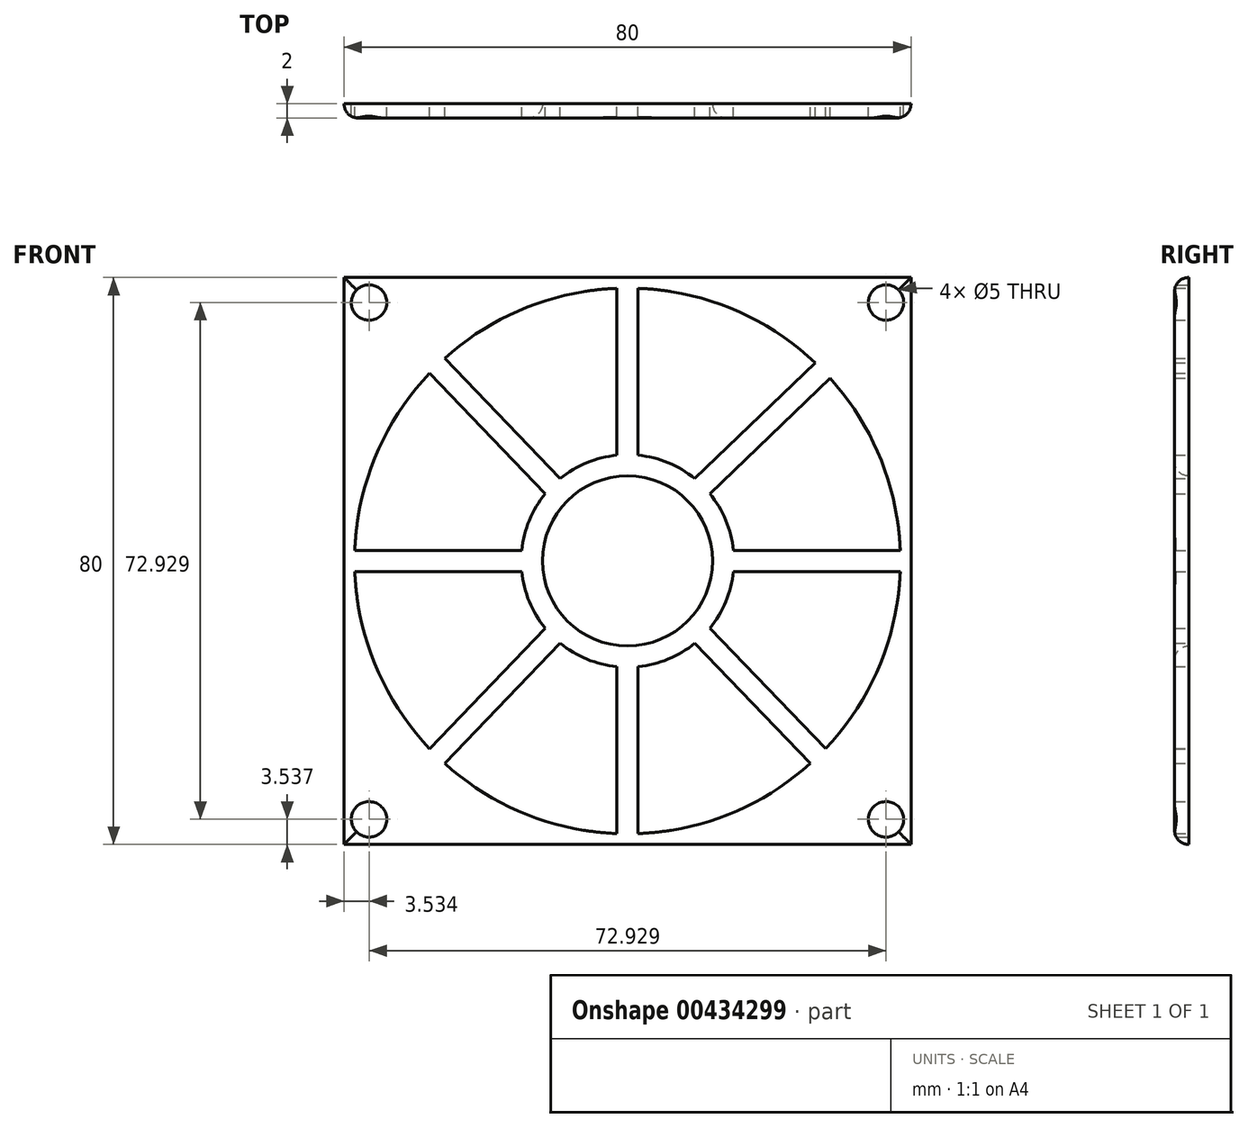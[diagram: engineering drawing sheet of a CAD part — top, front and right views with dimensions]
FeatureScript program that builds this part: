
annotation { "Feature Type Name" : "Feature", "Feature Type Description" : "" }
export const myFeature = defineFeature(function(context is Context, id is Id, definition is map)
    precondition{}
    {
        {
            var Q0;
            Q0=qCreatedBy(makeId("Front.planeOp"),FACE);
            var sketch = newSketch(context, id + "F0", { "sketchPlane" : qUnion([Q0])});
            skLineSegment(sketch, "E0.bottom", {"start": v(-40, 40.17) * mm, "end": v(40, 40.17) * mm});
            skLineSegment(sketch, "E0.top", {"start": v(-40, -39.83) * mm, "end": v(40, -39.83) * mm});
            skLineSegment(sketch, "E0.left", {"start": v(-40, 40.17) * mm, "end": v(-40, -39.83) * mm});
            skLineSegment(sketch, "E0.right", {"start": v(40, 40.17) * mm, "end": v(40, -39.83) * mm});
            skCircle(sketch, "E1", {"center": v(0, 0.17) * mm, "radius": 38.5 * mm});
            skCircle(sketch, "E2", {"center": v(0, 0.17) * mm, "radius": 15 * mm});
            skLineSegment(sketch, "E3", {"start": v(0, 38.67) * mm, "end": v(0, 15.17) * mm});
            skLineSegment(sketch, "E4", {"start": v(15, 0.17) * mm, "end": v(38.5, 0.17) * mm});
            skLineSegment(sketch, "E5", {"start": v(0, -14.83) * mm, "end": v(0, -38.33) * mm});
            skLineSegment(sketch, "E6", {"start": v(-15, 0.17) * mm, "end": v(-38.5, 0.17) * mm});
            skLineSegment(sketch, "E7", {"start": v(-1.5, -14.75) * mm, "end": v(-1.5, -38.3) * mm});
            skLineSegment(sketch, "E8", {"start": v(1.5, -14.75) * mm, "end": v(1.5, -38.3) * mm});
            skLineSegment(sketch, "E9", {"start": v(9.5, -11.44) * mm, "end": v(25.78, -28.42) * mm});
            skLineSegment(sketch, "E10", {"start": v(11.61, -9.32) * mm, "end": v(27.93, -26.33) * mm});
            skLineSegment(sketch, "E11", {"start": v(14.92, -1.33) * mm, "end": v(38.47, -1.33) * mm});
            skLineSegment(sketch, "E12", {"start": v(14.92, 1.67) * mm, "end": v(38.47, 1.67) * mm});
            skLineSegment(sketch, "E13", {"start": v(11.61, 9.67) * mm, "end": v(28.6, 25.95) * mm});
            skLineSegment(sketch, "E14", {"start": v(9.5, 11.79) * mm, "end": v(26.5, 28.1) * mm});
            skLineSegment(sketch, "E15", {"start": v(1.5, 15.1) * mm, "end": v(1.5, 38.64) * mm});
            skLineSegment(sketch, "E16", {"start": v(-1.5, 38.64) * mm, "end": v(-1.5, 15.1) * mm});
            skLineSegment(sketch, "E17", {"start": v(-9.5, 11.78) * mm, "end": v(-25.78, 28.76) * mm});
            skLineSegment(sketch, "E18", {"start": v(-11.62, 9.66) * mm, "end": v(-27.93, 26.67) * mm});
            skLineSegment(sketch, "E19", {"start": v(-14.93, 1.67) * mm, "end": v(-38.47, 1.67) * mm});
            skLineSegment(sketch, "E20", {"start": v(-14.93, -1.33) * mm, "end": v(-38.47, -1.33) * mm});
            skLineSegment(sketch, "E21", {"start": v(-9.5, -11.44) * mm, "end": v(-25.78, -28.42) * mm});
            skLineSegment(sketch, "E22", {"start": v(-11.61, -9.32) * mm, "end": v(-27.93, -26.33) * mm});
            skPoint(sketch, "E23", {"position": v(26.88, -27.4) * mm});
            skPoint(sketch, "E24", {"position": v(27.56, 27.05) * mm});
            skPoint(sketch, "E25", {"position": v(-26.88, 27.74) * mm});
            skPoint(sketch, "E26", {"position": v(-10.6, 10.78) * mm});
            skPoint(sketch, "E27", {"position": v(10.6, 10.78) * mm});
            skPoint(sketch, "E28", {"position": v(-10.6, -10.44) * mm});
            skPoint(sketch, "E29", {"position": v(10.6, -10.44) * mm});
            skPoint(sketch, "E30", {"position": v(-26.88, -27.4) * mm});
            skCircle(sketch, "E31", {"center": v(-36.47, -36.3) * mm, "radius": 2.5 * mm});
            skCircle(sketch, "E32", {"center": v(36.46, -36.3) * mm, "radius": 2.5 * mm});
            skCircle(sketch, "E33", {"center": v(36.46, 36.64) * mm, "radius": 2.5 * mm});
            skCircle(sketch, "E34", {"center": v(-36.47, 36.64) * mm, "radius": 2.5 * mm});
            skCircle(sketch, "E35", {"center": v(0, 0.17) * mm, "radius": 12 * mm});
            skSolve(sketch);
        }
        {
            var Q0;
            Q0=makeQuery(id+"F0.imprint","IMPRINT",FACE,{"disambiguationData":[TD([[makeQuery(id+"F0.imprint","IMPRINT",EDGE,{"derivedFrom":sQuery(id+"F0.wireOp",EDGE,"E0.bottom")}),-1.0]])]});
            var Q1;
            {var subQ0=sQuery(id+"F0.wireOp",EDGE,"E17");Q1=makeQuery(id+"F0.imprint","IMPRINT",FACE,{"disambiguationData":[TD([[makeQuery(id+"F0.imprint","IMPRINT",EDGE,{"derivedFrom":subQ0}),1.0]])]});}
            var Q2;
            Q2=makeQuery(id+"F0.imprint","IMPRINT",FACE,{"disambiguationData":[TD([[makeQuery(id+"F0.imprint","IMPRINT",EDGE,{"derivedFrom":sQuery(id+"F0.wireOp",EDGE,"E35")}),-1.0]])]});
            var Q3;
            {var subQ0=sQuery(id+"F0.wireOp",EDGE,"E3");Q3=makeQuery(id+"F0.imprint","IMPRINT",FACE,{"disambiguationData":[TD([[makeQuery(id+"F0.imprint","IMPRINT",EDGE,{"derivedFrom":subQ0}),-1.0]])]});}
            var Q4;
            {var subQ0=sQuery(id+"F0.wireOp",EDGE,"E3");Q4=makeQuery(id+"F0.imprint","IMPRINT",FACE,{"disambiguationData":[TD([[makeQuery(id+"F0.imprint","IMPRINT",EDGE,{"derivedFrom":subQ0}),1.0]])]});}
            var Q5;
            {var subQ0=sQuery(id+"F0.wireOp",EDGE,"E13");Q5=makeQuery(id+"F0.imprint","IMPRINT",FACE,{"disambiguationData":[TD([[makeQuery(id+"F0.imprint","IMPRINT",EDGE,{"derivedFrom":subQ0}),1.0]])]});}
            var Q6;
            {var subQ0=sQuery(id+"F0.wireOp",EDGE,"E4");Q6=makeQuery(id+"F0.imprint","IMPRINT",FACE,{"disambiguationData":[TD([[makeQuery(id+"F0.imprint","IMPRINT",EDGE,{"derivedFrom":subQ0}),1.0]])]});}
            var Q7;
            {var subQ0=sQuery(id+"F0.wireOp",EDGE,"E4");Q7=makeQuery(id+"F0.imprint","IMPRINT",FACE,{"disambiguationData":[TD([[makeQuery(id+"F0.imprint","IMPRINT",EDGE,{"derivedFrom":subQ0}),-1.0]])]});}
            var Q8;
            {var subQ0=sQuery(id+"F0.wireOp",EDGE,"E9");Q8=makeQuery(id+"F0.imprint","IMPRINT",FACE,{"disambiguationData":[TD([[makeQuery(id+"F0.imprint","IMPRINT",EDGE,{"derivedFrom":subQ0}),1.0]])]});}
            var Q9;
            {var subQ0=sQuery(id+"F0.wireOp",EDGE,"E5");Q9=makeQuery(id+"F0.imprint","IMPRINT",FACE,{"disambiguationData":[TD([[makeQuery(id+"F0.imprint","IMPRINT",EDGE,{"derivedFrom":subQ0}),1.0]])]});}
            var Q10;
            {var subQ0=sQuery(id+"F0.wireOp",EDGE,"E5");Q10=makeQuery(id+"F0.imprint","IMPRINT",FACE,{"disambiguationData":[TD([[makeQuery(id+"F0.imprint","IMPRINT",EDGE,{"derivedFrom":subQ0}),-1.0]])]});}
            var Q11;
            {var subQ0=sQuery(id+"F0.wireOp",EDGE,"E21");Q11=makeQuery(id+"F0.imprint","IMPRINT",FACE,{"disambiguationData":[TD([[makeQuery(id+"F0.imprint","IMPRINT",EDGE,{"derivedFrom":subQ0}),-1.0]])]});}
            var Q12;
            {var subQ0=sQuery(id+"F0.wireOp",EDGE,"E6");Q12=makeQuery(id+"F0.imprint","IMPRINT",FACE,{"disambiguationData":[TD([[makeQuery(id+"F0.imprint","IMPRINT",EDGE,{"derivedFrom":subQ0}),1.0]])]});}
            var Q13;
            {var subQ0=sQuery(id+"F0.wireOp",EDGE,"E6");Q13=makeQuery(id+"F0.imprint","IMPRINT",FACE,{"disambiguationData":[TD([[makeQuery(id+"F0.imprint","IMPRINT",EDGE,{"derivedFrom":subQ0}),-1.0]])]});}
            extrude(context, id + "F1", {"entities" : qUnion([Q0, Q1, Q2, Q3, Q4, Q5, Q6, Q7, Q8, Q9, Q10, Q11, Q12, Q13]), "depth" : 2 * mm, "offsetDistance" : 25 * mm});
        }
        {
            var Q0;
            Q0=makeQuery(id+"F1.opExtrude","CAP_EDGE",EDGE,{"disambiguationData":[OSD([sQuery(id+"F0.wireOp",EDGE,"E0.bottom")])],"isStart":false});
            var Q1;
            Q1=makeQuery(id+"F1.opExtrude","CAP_EDGE",EDGE,{"disambiguationData":[OSD([sQuery(id+"F0.wireOp",EDGE,"E0.right")])],"isStart":false});
            var Q2;
            Q2=makeQuery(id+"F1.opExtrude","CAP_EDGE",EDGE,{"disambiguationData":[OSD([sQuery(id+"F0.wireOp",EDGE,"E0.top")])],"isStart":false});
            var Q3;
            Q3=makeQuery(id+"F1.opExtrude","CAP_EDGE",EDGE,{"disambiguationData":[OSD([sQuery(id+"F0.wireOp",EDGE,"E0.left")])],"isStart":false});
            var Q4;
            Q4=makeQuery(id+"F1.opExtrude","CAP_EDGE",EDGE,{"disambiguationData":[OSD([sQuery(id+"F0.wireOp",EDGE,"E35")])],"isStart":false});
            fillet(context, id + "F2", {"entities" : qUnion([Q0, Q1, Q2, Q3, Q4]), "radius" : 2 * mm, "tangentPropagation" : true, "allowEdgeOverflow" : false});
        }
    });
